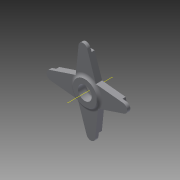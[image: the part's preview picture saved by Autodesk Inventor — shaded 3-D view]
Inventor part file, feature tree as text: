
AUTODESK INVENTOR PART (.ipt)
format: ipt  version: 2015 (Build 190159000, 159)  size: 167,936 bytes
history: native  units: mm
features: sketch x3, other x3, extrude x2, pattern_circular x2, projected_geometry x2, hole x1, revolve x1, fillet x1
ambient origin geometry x8: Origin, YZ Plane, XZ Plane, XY Plane, X Axis, Y Axis, Z Axis, Center Point
bodies: Solid1 (feature_tree)
feature tree (15):
  extrude  "Extrusion1"  Depth=3.0mm TaperAngle=0.0deg
  extrude  "Extrusion2"  Depth=10.0mm
  pattern_circular  "Circular Pattern1"  Count=4 Angle=360.0deg
  hole  "Hole1"  [1 undecoded]
  pattern_circular  "Circular Pattern2"  [2 undecoded]
  revolve  "Revolution1"  [1 undecoded]
  fillet  "Fillet1"  Radius=6.705576mm
  sketch  "Sketch1"  dims[d0=5.0mm d1=0.0mm d2=3.0mm d3=0.0mm]
  sketch  "Sketch2"  dims[d4=40.0mm d5=360.0deg d7=10.0mm d8=10.0mm]
  other  "Work Axis1"
  other  "Work Axis2"
  other  "Work Axis3"
  sketch  "Sketch3"  dims[d9=1.5mm d10=6.0mm d11=4.0mm d12=2.0mm d13=90.0deg d14=8.0mm d15=20.594885mm d16=40.0mm d17=360.0deg d19=90.0deg d20=2.0mm d21=11.676532mm d22=6.705576mm d23=2.188916mm d24=4.213231mm]
  projected_geometry  "Projected Loop1"
  projected_geometry  "Projected Loop2"
note: 4 required parameter values undecoded (feature->parameter linkage not recoverable at this tier; creation-order binding heuristic only, values carry confidence <= 0.55)